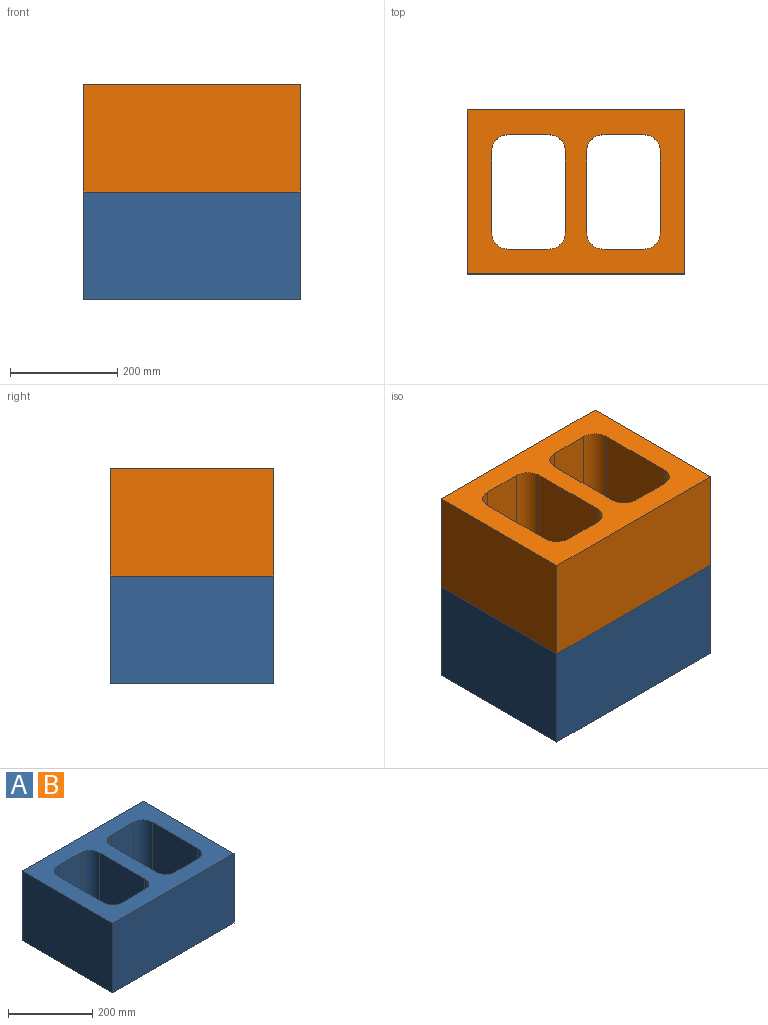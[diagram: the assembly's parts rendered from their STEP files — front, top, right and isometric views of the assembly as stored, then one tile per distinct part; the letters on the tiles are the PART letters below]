
ASSEMBLY  parts=2 mates=1
PART A: 22 faces, bbox 405.4x304.8x201.2 mm
  f0: plane 304.8x201.17mm, normal (-1,0,0), area 61316mm2, adj f1,f3,f4,f5
  f1: plane 405.38x201.17mm, normal (0,-1,0), area 81550.3mm2, adj f0,f2,f4,f5
  f2: plane 304.8x201.17mm, normal (1,0,0), area 61316mm2, adj f1,f3,f4,f5
  f3: plane 405.38x201.17mm, normal (0,1,0), area 81550.3mm2, adj f0,f2,f4,f5
  f4: plane 405.38x304.8mm, normal (0,0,1), area 66627.1mm2, adj f0,f1,f2,f3,f6,f7,f8,f9
  f5: plane 405.38x304.8mm, normal (0,0,-1), area 66627.1mm2, adj f0,f1,f2,f3,f6,f7,f8,f9
  f6: plane 201.17x152.4mm, normal (1,0,0), area 30658mm2, adj f4,f5,f18,f21
  f7: plane 201.17x76.2mm, normal (0,-1,0), area 15329mm2, adj f4,f5,f18,f19
  f8: plane 201.17x152.4mm, normal (-1,0,0), area 30658mm2, adj f4,f5,f19,f20
  f9: plane 201.17x76.2mm, normal (0,1,0), area 15329mm2, adj f4,f5,f20,f21
  f10: plane 201.17x152.4mm, normal (1,0,0), area 30658mm2, adj f4,f5,f14,f17
  f11: plane 201.17x76.2mm, normal (0,-1,0), area 15329mm2, adj f4,f5,f16,f17
  f12: plane 201.17x152.4mm, normal (-1,0,0), area 30658mm2, adj f4,f5,f15,f16
  f13: plane 201.17x76.2mm, normal (0,1,0), area 15329mm2, adj f4,f5,f14,f15
  f14: cylinder r=30.48mm len=201.17mm, axis (0,0,-1), area 9631.5mm2, adj f4,f5,f10,f13
  f15: cylinder r=30.48mm len=201.17mm, axis (0,0,1), area 9631.5mm2, adj f4,f5,f12,f13
  f16: cylinder r=30.48mm len=201.17mm, axis (0,0,-1), area 9631.5mm2, adj f4,f5,f11,f12
  f17: cylinder r=30.48mm len=201.17mm, axis (0,0,1), area 9631.5mm2, adj f4,f5,f10,f11
  f18: cylinder r=30.48mm len=201.17mm, axis (0,0,1), area 9631.5mm2, adj f4,f5,f6,f7
  f19: cylinder r=30.48mm len=201.17mm, axis (0,0,-1), area 9631.5mm2, adj f4,f5,f7,f8
  f20: cylinder r=30.48mm len=201.17mm, axis (0,0,1), area 9631.5mm2, adj f4,f5,f8,f9
  f21: cylinder r=30.48mm len=201.17mm, axis (0,0,-1), area 9631.5mm2, adj f4,f5,f6,f9
PART B: same geometry as A
PLACE A t=(0,-339.12,-201.17)mm
PLACE B t=(0,-339.12,0)mm
MATE fastened A.f4 <-> B.f5  axis (0,0,1) through (405.38,-339.12,0)mm
